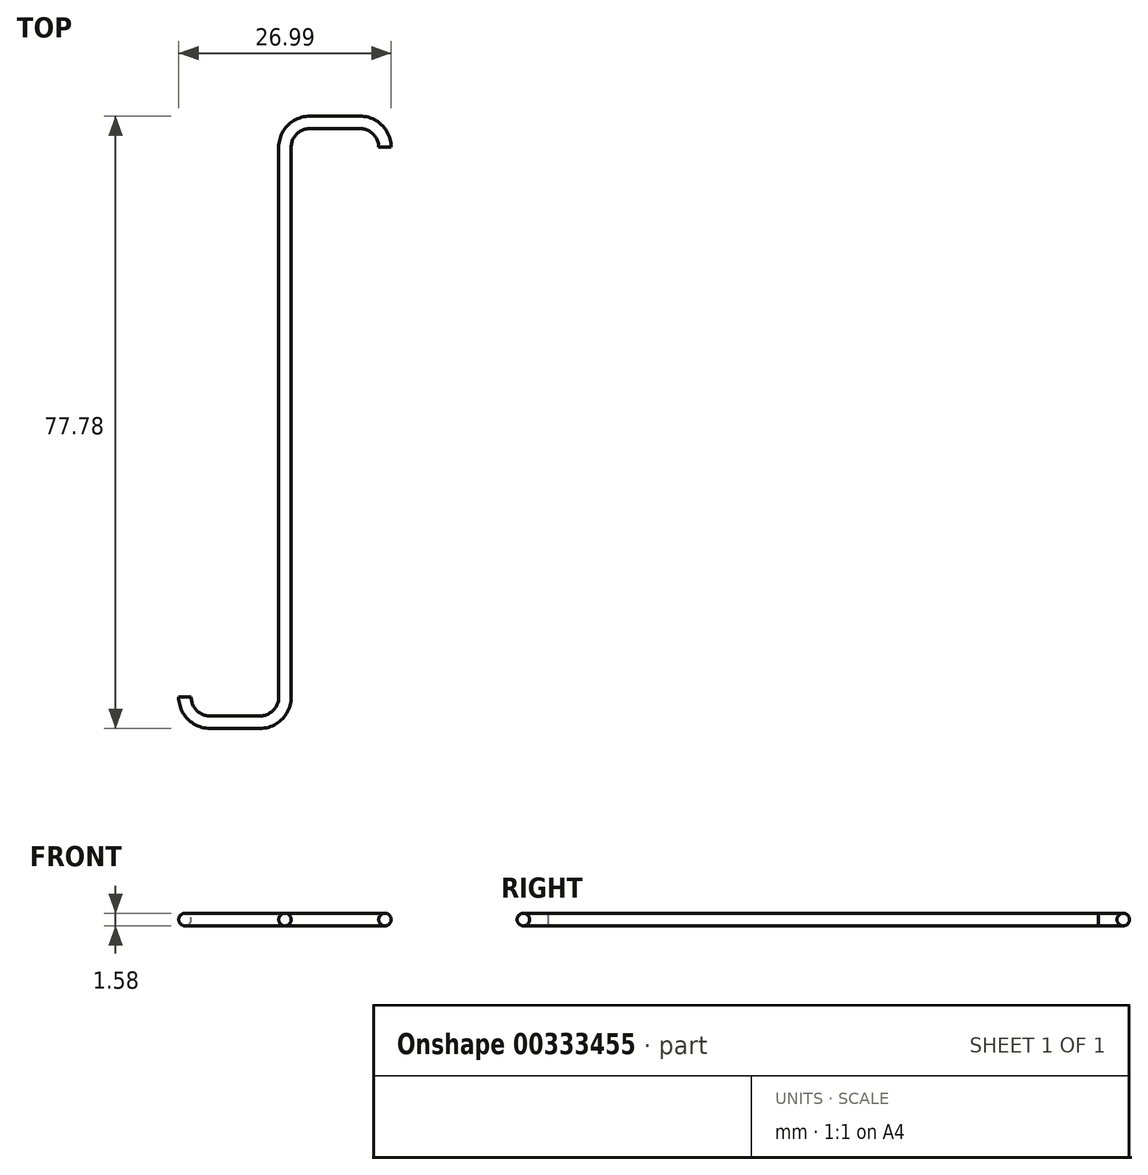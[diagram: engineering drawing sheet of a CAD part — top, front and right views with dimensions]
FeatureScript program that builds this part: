
annotation { "Feature Type Name" : "Feature", "Feature Type Description" : "" }
export const myFeature = defineFeature(function(context is Context, id is Id, definition is map)
    precondition{}
    {
        {
            var Q0;
            Q0=qCreatedBy(makeId("Top.planeOp"),FACE);
            var sketch = newSketch(context, id + "F0", { "sketchPlane" : qUnion([Q0])});
            skLineSegment(sketch, "E0", {"start": v(0, 0) * mm, "end": v(-6.35, 0) * mm});
            skLineSegment(sketch, "E1", {"start": v(6.35, 76.2) * mm, "end": v(12.7, 76.2) * mm});
            skArc(sketch, "E2", {"start": v(0, 0) * mm, "mid": v(2.25, 0.93) * mm, "end": v(3.18, 3.18) * mm});
            skArc(sketch, "E3", {"start": v(6.35, 76.2) * mm, "mid": v(4.1, 75.27) * mm, "end": v(3.17, 73.03) * mm});
            skLineSegment(sketch, "E4", {"start": v(3.18, 3.18) * mm, "end": v(3.18, 73.03) * mm});
            skArc(sketch, "E5", {"start": v(15.88, 73.03) * mm, "mid": v(14.95, 75.27) * mm, "end": v(12.7, 76.2) * mm});
            skArc(sketch, "E6", {"start": v(-9.53, 3.17) * mm, "mid": v(-8.6, 0.93) * mm, "end": v(-6.35, 0) * mm});
            skSolve(sketch);
        }
        {
            var Q0;
            Q0=qCreatedBy(makeId("Right.planeOp"),FACE);
            var Q1;
            Q1=sQuery(id+"F0.wireOp",VERTEX,"E0.end");
            cPlane(context, id + "F1", {"entities" : qUnion([Q0, Q1]), "cplaneType" : CPlaneType.PLANE_POINT, "offset" : 25.4 * mm, "width" : 152.4 * mm, "height" : 152.4 * mm});
        }
        {
            var Q0;
            Q0=qCreatedBy(id+"F1.planeOp",FACE);
            var sketch = newSketch(context, id + "F2", { "sketchPlane" : qUnion([Q0])});
            skCircle(sketch, "E7", {"center": v(0, 0) * mm, "radius": 0.8 * mm});
            skSolve(sketch);
        }
        {
            var Q0;
            Q0=makeQuery(id+"F2.imprint","IMPRINT",FACE,{"disambiguationData":[TD([[makeQuery(id+"F2.imprint","IMPRINT",EDGE,{"derivedFrom":sQuery(id+"F2.wireOp",EDGE,"E7")}),1.0]])]});
            var Q1;
            Q1=sQuery(id+"F0.wireOp",EDGE,"E0");
            var Q2;
            Q2=sQuery(id+"F0.wireOp",EDGE,"E2");
            var Q3;
            Q3=sQuery(id+"F0.wireOp",EDGE,"E4");
            var Q4;
            Q4=sQuery(id+"F0.wireOp",EDGE,"E3");
            var Q5;
            Q5=sQuery(id+"F0.wireOp",EDGE,"E1");
            var Q6;
            Q6=sQuery(id+"F0.wireOp",EDGE,"E5");
            sweep(context, id + "F3", {"profiles" : qUnion([Q0]), "path" : qUnion([Q1, Q2, Q3, Q4, Q5, Q6])});
        }
        {
            var Q0;
            Q0=makeQuery(id+"F2.imprint","IMPRINT",FACE,{"disambiguationData":[TD([[makeQuery(id+"F2.imprint","IMPRINT",EDGE,{"derivedFrom":sQuery(id+"F2.wireOp",EDGE,"E7")}),1.0]])]});
            var Q1;
            Q1=sQuery(id+"F0.wireOp",EDGE,"E6");
            sweep(context, id + "F4", {"operationType" : NewBodyOperationType.ADD, "profiles" : qUnion([Q0]), "path" : qUnion([Q1])});
        }
    });
